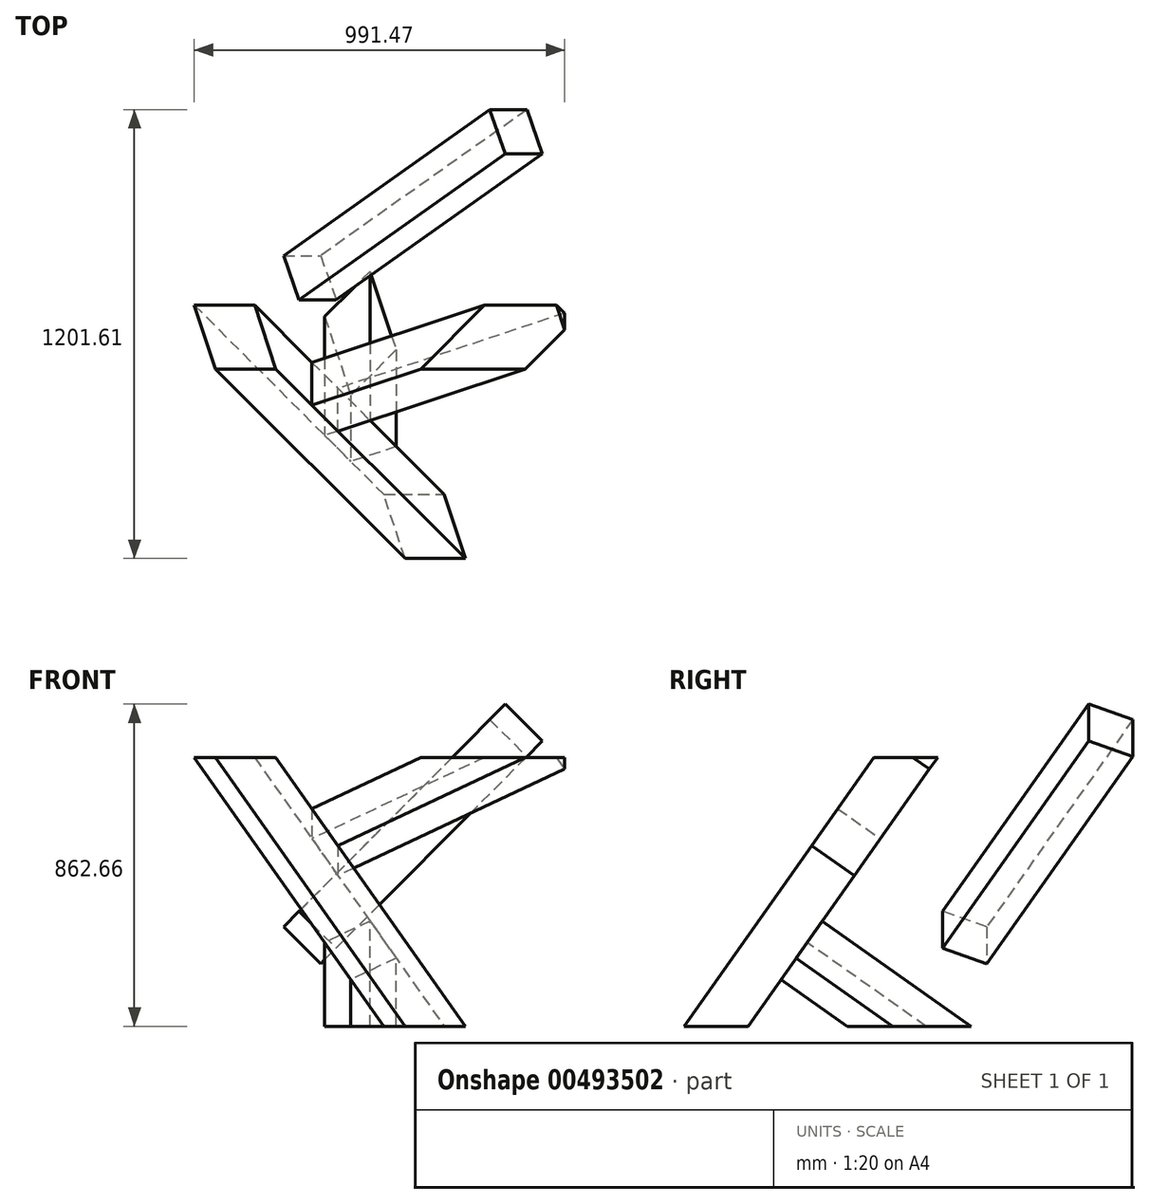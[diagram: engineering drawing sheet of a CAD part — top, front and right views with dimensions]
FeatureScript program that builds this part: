
annotation { "Feature Type Name" : "Feature", "Feature Type Description" : "" }
export const myFeature = defineFeature(function(context is Context, id is Id, definition is map)
    precondition{}
    {
        {
            var Q0;
            Q0=qCreatedBy(makeId("Top.planeOp"),FACE);
            var sketch = newSketch(context, id + "F0", { "sketchPlane" : qUnion([Q0])});
            skLineSegment(sketch, "E0.bottom", {"start": v(400, 400) * mm, "end": v(-400, 400) * mm, "construction": true});
            skLineSegment(sketch, "E0.top", {"start": v(400, -400) * mm, "end": v(-400, -400) * mm, "construction": true});
            skLineSegment(sketch, "E0.left", {"start": v(400, 400) * mm, "end": v(400, -400) * mm, "construction": true});
            skLineSegment(sketch, "E0.right", {"start": v(-400, 400) * mm, "end": v(-400, -400) * mm, "construction": true});
            skPoint(sketch, "E0.middle", {"position": v(0, 0) * mm});
            skPoint(sketch, "E1", {"position": v(250, -314) * mm});
            skSolve(sketch);
        }
        {
            var Q0;
            Q0=qCreatedBy(makeId("Top.planeOp"),FACE);
            cPlane(context, id + "F1", {"entities" : qUnion([Q0]), "cplaneType" : CPlaneType.OFFSET, "offset" : 800 * mm, "width" : 150 * mm, "height" : 150 * mm});
        }
        {
            var Q0;
            Q0=qCreatedBy(id+"F1.planeOp",FACE);
            var sketch = newSketch(context, id + "F2", { "sketchPlane" : qUnion([Q0])});
            skLineSegment(sketch, "E2.0", {"start": v(-400, 400) * mm, "end": v(-400, -400) * mm, "construction": true});
            skLineSegment(sketch, "E2.1", {"start": v(400, 400) * mm, "end": v(-400, 400) * mm, "construction": true});
            skLineSegment(sketch, "E2.2", {"start": v(400, 400) * mm, "end": v(400, -400) * mm, "construction": true});
            skLineSegment(sketch, "E2.3", {"start": v(400, -400) * mm, "end": v(-400, -400) * mm, "construction": true});
            skPoint(sketch, "E3", {"position": v(-314, 250) * mm});
            skSolve(sketch);
        }
        {
            var Q0;
            Q0=sQuery(id+"F2.wireOp",VERTEX,"E3");
            var Q1;
            Q1=sQuery(id+"F0.wireOp",VERTEX,"E1");
            var Q2;
            Q2=sQuery(id+"F2.wireOp",VERTEX,"E2.2.end");
            cPlane(context, id + "F3", {"entities" : qUnion([Q0, Q1, Q2]), "cplaneType" : CPlaneType.THREE_POINT, "offset" : 25 * mm, "width" : 150 * mm, "height" : 150 * mm});
        }
        {
            var Q0;
            Q0=qCreatedBy(id+"F3.planeOp",FACE);
            var sketch = newSketch(context, id + "F4", { "sketchPlane" : qUnion([Q0])});
            skPoint(sketch, "E4.0", {"position": v(366.25, 814.17) * mm});
            skPoint(sketch, "E5.0", {"position": v(-395.76, -19.8) * mm});
            skLineSegment(sketch, "E6", {"start": v(366.25, 814.17) * mm, "end": v(-395.76, -19.8) * mm});
            skLineSegment(sketch, "E7.0", {"start": v(329.34, 847.9) * mm, "end": v(-432.68, 13.92) * mm, "construction": true});
            skSolve(sketch);
        }
        {
            var Q0;
            Q0=sQuery(id+"F4.wireOp",EDGE,"E6");
            cPlane(context, id + "F5", {"entities" : qUnion([Q0]), "cplaneType" : CPlaneType.LINE_ANGLE, "offset" : 25 * mm, "angle" : 0 * degree, "width" : 150 * mm, "height" : 150 * mm});
        }
        {
            var Q0;
            Q0=qCreatedBy(id+"F5.planeOp",FACE);
            var sketch = newSketch(context, id + "F6", { "sketchPlane" : qUnion([Q0])});
            skLineSegment(sketch, "E8.0", {"start": v(-293.32, 809.81) * mm, "end": v(270.68, -169.01) * mm, "construction": true});
            skSolve(sketch);
        }
        {
            var Q0;
            Q0=sQuery(id+"F4.wireOp",VERTEX,"E7.0.start");
            var Q1;
            Q1=sQuery(id+"F4.wireOp",VERTEX,"E4.0");
            var Q2;
            Q2=sQuery(id+"F6.wireOp",VERTEX,"E8.0.start");
            cPlane(context, id + "F7", {"entities" : qUnion([Q0, Q1, Q2]), "cplaneType" : CPlaneType.THREE_POINT, "offset" : 25 * mm, "width" : 150 * mm, "height" : 150 * mm});
        }
        {
            var Q0;
            Q0=qCreatedBy(id+"F7.planeOp",FACE);
            cPlane(context, id + "F8", {"entities" : qUnion([Q0]), "cplaneType" : CPlaneType.OFFSET, "offset" : 565 * mm, "oppositeDirection" : true, "width" : 150 * mm, "height" : 150 * mm});
        }
        {
            var Q0;
            Q0=qCreatedBy(id+"F8.planeOp",FACE);
            var sketch = newSketch(context, id + "F9", { "sketchPlane" : qUnion([Q0])});
            skPoint(sketch, "E9.0", {"position": v(126.29, -256.63) * mm});
            skLineSegment(sketch, "E10.bottom", {"start": v(196.29, -186.63) * mm, "end": v(56.29, -186.63) * mm});
            skLineSegment(sketch, "E10.top", {"start": v(196.29, -326.63) * mm, "end": v(56.29, -326.63) * mm});
            skLineSegment(sketch, "E10.left", {"start": v(196.29, -186.63) * mm, "end": v(196.29, -326.63) * mm});
            skLineSegment(sketch, "E10.right", {"start": v(56.29, -186.63) * mm, "end": v(56.29, -326.63) * mm});
            skSolve(sketch);
        }
        {
            var Q0;
            Q0 = qSketchRegion(id + "F9", true);
            extrude(context, id + "F10", {"entities" : qUnion([Q0]), "depth" : 800 * mm, "hasSecondDirection" : true, "secondDirectionOppositeDirection" : true, "secondDirectionDepth" : 800 * mm});
        }
        {
            var Q0;
            Q0=qCreatedBy(makeId("Right.planeOp"),FACE);
            cPlane(context, id + "F11", {"entities" : qUnion([Q0]), "cplaneType" : CPlaneType.OFFSET, "offset" : 1000 * mm, "oppositeDirection" : true, "width" : 150 * mm, "height" : 150 * mm});
        }
        {
            var Q0;
            Q0=qCreatedBy(id+"F11.planeOp",FACE);
            var sketch = newSketch(context, id + "F12", { "sketchPlane" : qUnion([Q0])});
            skLineSegment(sketch, "E11.0", {"start": v(564.6, 800) * mm, "end": v(0, 800) * mm});
            skLineSegment(sketch, "E12.0", {"start": v(-127.97, 0) * mm, "end": v(-400, 0) * mm});
            skLineSegment(sketch, "E13", {"start": v(564.6, 800) * mm, "end": v(564.6, 1085.03) * mm});
            skLineSegment(sketch, "E14", {"start": v(564.6, 1085.03) * mm, "end": v(0, 1085.03) * mm});
            skLineSegment(sketch, "E15", {"start": v(0, 1085.03) * mm, "end": v(0, 800) * mm});
            skPoint(sketch, "E16.orphan", {"position": v(400, 800) * mm});
            skPoint(sketch, "E17.orphan", {"position": v(-400, 800) * mm});
            skLineSegment(sketch, "E18", {"start": v(-400, 0) * mm, "end": v(-567.88, 0) * mm});
            skLineSegment(sketch, "E19", {"start": v(-567.88, 0) * mm, "end": v(-567.88, -303.64) * mm});
            skLineSegment(sketch, "E20", {"start": v(-567.88, -303.64) * mm, "end": v(-127.97, -303.64) * mm});
            skLineSegment(sketch, "E21", {"start": v(-127.97, -303.64) * mm, "end": v(-127.97, 0) * mm});
            skPoint(sketch, "E22.orphan", {"position": v(400, 0) * mm});
            skSolve(sketch);
        }
        {
            var Q0;
            Q0 = qSketchRegion(id + "F12", true);
            extrude(context, id + "F13", {"entities" : qUnion([Q0]), "operationType" : NewBodyOperationType.REMOVE, "endBound" : BoundingType.THROUGH_ALL, "depth" : 25 * mm});
        }
        {
            var Q0;
            Q0=makeQuery(id+"F10.opExtrude","SWEPT_FACE",FACE,{"disambiguationData":[OSD([sQuery(id+"F9.wireOp",EDGE,"E10.bottom")])]});
            var sketch = newSketch(context, id + "F14", { "sketchPlane" : qUnion([Q0])});
            skLineSegment(sketch, "E23.0", {"start": v(-75.7, 261.8) * mm, "end": v(-145.59, 140.49) * mm});
            skLineSegment(sketch, "E24.0", {"start": v(45.61, 191.9) * mm, "end": v(-24.28, 70.6) * mm});
            skLineSegment(sketch, "E25", {"start": v(-145.59, 140.49) * mm, "end": v(-24.28, 70.6) * mm});
            skLineSegment(sketch, "E26.0", {"start": v(-75.7, 261.8) * mm, "end": v(45.61, 191.9) * mm});
            skPoint(sketch, "E27.orphan", {"position": v(261.65, 847.25) * mm});
            skPoint(sketch, "E28.orphan", {"position": v(423.22, 847.25) * mm});
            skPoint(sketch, "E29.orphan", {"position": v(-140.78, -131.58) * mm});
            skPoint(sketch, "E30.orphan", {"position": v(-302.35, -131.58) * mm});
            skSolve(sketch);
        }
        {
            var Q0;
            Q0 = qSketchRegion(id + "F14", true);
            extrude(context, id + "F15", {"entities" : qUnion([Q0]), "depth" : 700 * mm});
        }
        {
            var Q0;
            Q0=qCreatedBy(id+"F11.planeOp",FACE);
            var sketch = newSketch(context, id + "F16", { "sketchPlane" : qUnion([Q0])});
            skLineSegment(sketch, "E31.bottom", {"start": v(655.93, 0) * mm, "end": v(95.03, 0) * mm});
            skLineSegment(sketch, "E31.top", {"start": v(655.93, -273.26) * mm, "end": v(95.03, -273.26) * mm});
            skLineSegment(sketch, "E31.left", {"start": v(655.93, 0) * mm, "end": v(655.93, -273.26) * mm});
            skLineSegment(sketch, "E31.right", {"start": v(95.03, 0) * mm, "end": v(95.03, -273.26) * mm});
            skSolve(sketch);
        }
        {
            var Q0;
            Q0 = qSketchRegion(id + "F16", true);
            extrude(context, id + "F17", {"entities" : qUnion([Q0]), "operationType" : NewBodyOperationType.REMOVE, "endBound" : BoundingType.THROUGH_ALL, "depth" : 25 * mm});
        }
        {
            var Q0;
            Q0=makeQuery(id+"F10.opExtrude","SWEPT_FACE",FACE,{"disambiguationData":[OSD([sQuery(id+"F9.wireOp",EDGE,"E10.left")])]});
            var sketch = newSketch(context, id + "F18", { "sketchPlane" : qUnion([Q0])});
            skLineSegment(sketch, "E32.0", {"start": v(112.65, 811) * mm, "end": v(-476.24, -153.05) * mm});
            skLineSegment(sketch, "E33.0", {"start": v(291.5, 835.23) * mm, "end": v(-297.39, -128.82) * mm});
            skLineSegment(sketch, "E34", {"start": v(-90.65, 478.19) * mm, "end": v(28.82, 405.2) * mm});
            skLineSegment(sketch, "E35", {"start": v(-17.67, 597.66) * mm, "end": v(101.8, 524.68) * mm});
            skSolve(sketch);
        }
        {
            var Q0;
            {var subQ0=sQuery(id+"F18.wireOp",EDGE,"E34");Q0=makeQuery(id+"F18.imprint","IMPRINT",FACE,{"disambiguationData":[TD([[makeQuery(id+"F18.imprint","IMPRINT",EDGE,{"derivedFrom":subQ0}),1.0]])]});}
            extrude(context, id + "F19", {"entities" : qUnion([Q0]), "depth" : 700 * mm});
        }
        {
            var Q0;
            Q0=qCreatedBy(id+"F11.planeOp",FACE);
            var sketch = newSketch(context, id + "F20", { "sketchPlane" : qUnion([Q0])});
            skLineSegment(sketch, "E36.0", {"start": v(468.48, 800) * mm, "end": v(400, 800) * mm});
            skLineSegment(sketch, "E37", {"start": v(468.48, 800) * mm, "end": v(468.48, 1033.91) * mm});
            skLineSegment(sketch, "E38", {"start": v(468.48, 1033.91) * mm, "end": v(129.15, 1033.91) * mm});
            skLineSegment(sketch, "E39", {"start": v(129.15, 1033.91) * mm, "end": v(129.15, 800) * mm});
            skPoint(sketch, "E40.orphan", {"position": v(400, 800) * mm});
            skPoint(sketch, "E41.orphan", {"position": v(-400, 800) * mm});
            skLineSegment(sketch, "E42", {"start": v(400, 800) * mm, "end": v(129.15, 800) * mm});
            skSolve(sketch);
        }
        {
            var Q0;
            Q0 = qSketchRegion(id + "F20", true);
            extrude(context, id + "F21", {"entities" : qUnion([Q0]), "operationType" : NewBodyOperationType.REMOVE, "endBound" : BoundingType.THROUGH_ALL, "depth" : 25 * mm});
        }
        {
            var Q0;
            Q0=qCreatedBy(id+"F11.planeOp",FACE);
            var sketch = newSketch(context, id + "F22", { "sketchPlane" : qUnion([Q0])});
            skLineSegment(sketch, "E43.0", {"start": v(400, 800) * mm, "end": v(-400, 800) * mm, "construction": true});
            skLineSegment(sketch, "E44.0", {"start": v(400, 0) * mm, "end": v(-400, 0) * mm, "construction": true});
            skLineSegment(sketch, "E45.0", {"start": v(400, 760) * mm, "end": v(-400, 760) * mm});
            skLineSegment(sketch, "E46.0", {"start": v(497.86, 40) * mm, "end": v(-483.43, 40) * mm});
            skLineSegment(sketch, "E47", {"start": v(400, 760) * mm, "end": v(400, 856.38) * mm});
            skLineSegment(sketch, "E48", {"start": v(400, 856.38) * mm, "end": v(-400, 856.38) * mm});
            skLineSegment(sketch, "E49", {"start": v(-400, 856.38) * mm, "end": v(-400, 760) * mm});
            skLineSegment(sketch, "E50", {"start": v(497.86, 40) * mm, "end": v(497.86, -63.05) * mm});
            skLineSegment(sketch, "E51", {"start": v(497.86, -63.05) * mm, "end": v(-483.43, -63.05) * mm});
            skLineSegment(sketch, "E52", {"start": v(-483.43, -63.05) * mm, "end": v(-483.43, 40) * mm});
            skPoint(sketch, "E53.orphan", {"position": v(400, 40) * mm});
            skPoint(sketch, "E54.orphan", {"position": v(-400, 40) * mm});
            skSolve(sketch);
        }
        {
            var Q0;
            Q0 = qSketchRegion(id + "F22", true);
            extrude(context, id + "F23", {"entities" : qUnion([Q0]), "operationType" : NewBodyOperationType.REMOVE, "endBound" : BoundingType.THROUGH_ALL, "depth" : 25 * mm});
        }
        {
            var Q0;
            Q0=makeQuery(id+"F10.opExtrude","SWEPT_FACE",FACE,{"disambiguationData":[OSD([sQuery(id+"F9.wireOp",EDGE,"E10.left")])]});
            var sketch = newSketch(context, id + "F24", { "sketchPlane" : qUnion([Q0])});
            skLineSegment(sketch, "E55.0", {"start": v(-47.12, 549.46) * mm, "end": v(-120.62, 429.13) * mm});
            skLineSegment(sketch, "E55.1", {"start": v(72.36, 476.48) * mm, "end": v(-1.15, 356.15) * mm});
            skLineSegment(sketch, "E56", {"start": v(-47.12, 549.46) * mm, "end": v(72.36, 476.48) * mm});
            skLineSegment(sketch, "E57.0", {"start": v(-120.62, 429.13) * mm, "end": v(-1.15, 356.15) * mm});
            skPoint(sketch, "E58.orphan", {"position": v(83.2, 762.8) * mm});
            skPoint(sketch, "E59.orphan", {"position": v(262.06, 787.03) * mm});
            skPoint(sketch, "E60.orphan", {"position": v(-267.94, -80.62) * mm});
            skPoint(sketch, "E61.orphan", {"position": v(-446.8, -104.85) * mm});
            skSolve(sketch);
        }
        {
            var Q0;
            Q0=makeQuery(id+"F10.opExtrude","SWEPT_FACE",FACE,{"disambiguationData":[OSD([sQuery(id+"F9.wireOp",EDGE,"E10.top")])]});
            var sketch = newSketch(context, id + "F25", { "sketchPlane" : qUnion([Q0])});
            skLineSegment(sketch, "E62.0", {"start": v(-51.76, 483) * mm, "end": v(18.63, 360.82) * mm});
            skLineSegment(sketch, "E63", {"start": v(-51.76, 483) * mm, "end": v(56.82, 394.62) * mm});
            skLineSegment(sketch, "E64", {"start": v(56.82, 394.62) * mm, "end": v(18.63, 360.82) * mm});
            skSolve(sketch);
        }
        {
            var Q0;
            Q0=sQuery(id+"F24.wireOp",VERTEX,"E56.end");
            var Q1;
            Q1=sQuery(id+"F25.wireOp",VERTEX,"E63.start");
            var Q2;
            Q2=sQuery(id+"F25.wireOp",VERTEX,"E64.start");
            cPlane(context, id + "F26", {"entities" : qUnion([Q0, Q1, Q2]), "cplaneType" : CPlaneType.THREE_POINT, "offset" : 25 * mm, "width" : 150 * mm, "height" : 150 * mm});
        }
        {
            var Q0;
            Q0=qCreatedBy(id+"F26.planeOp",FACE);
            var sketch = newSketch(context, id + "F27", { "sketchPlane" : qUnion([Q0])});
            skLineSegment(sketch, "E65.0", {"start": v(-345.02, 326.63) * mm, "end": v(-345.02, 186.63) * mm});
            skLineSegment(sketch, "E65.1", {"start": v(-345.02, 326.63) * mm, "end": v(-205.02, 326.63) * mm});
            skLineSegment(sketch, "E66.0", {"start": v(-345.02, 186.63) * mm, "end": v(-213.3, 186.63) * mm});
            skLineSegment(sketch, "E67.0", {"start": v(-213.3, 326.63) * mm, "end": v(-213.3, 186.63) * mm});
            skSolve(sketch);
        }
        {
            var Q0;
            Q0=makeQuery(id+"F27.imprint","IMPRINT",FACE,{"disambiguationData":[TD([[makeQuery(id+"F27.imprint","IMPRINT",EDGE,{"derivedFrom":sQuery(id+"F27.wireOp",EDGE,"E65.0")}),1.0]])]});
            extrude(context, id + "F28", {"entities" : qUnion([Q0]), "operationType" : NewBodyOperationType.ADD, "oppositeDirection" : true, "depth" : 25 * mm, "hasSecondDirection" : true, "secondDirectionOppositeDirection" : false, "secondDirectionDepth" : 50 * mm});
        }
        {
            var Q0;
            Q0=makeQuery(id+"F28.opExtrude","CAP_FACE",FACE,{"disambiguationData":[OSD([sQuery(id+"F27.wireOp",EDGE,"E65.0"),sQuery(id+"F27.wireOp",EDGE,"E65.1"),sQuery(id+"F27.wireOp",EDGE,"E66.0"),sQuery(id+"F27.wireOp",EDGE,"E67.0")])],"isStart":false});
            extrude(context, id + "F29", {"entities" : qUnion([Q0]), "operationType" : NewBodyOperationType.ADD, "depth" : 800 * mm});
        }
        {
            var Q0;
            Q0=qCreatedBy(id+"F11.planeOp",FACE);
            var sketch = newSketch(context, id + "F30", { "sketchPlane" : qUnion([Q0])});
            skLineSegment(sketch, "E68.0", {"start": v(136.15, 760) * mm, "end": v(307.45, 760) * mm});
            skLineSegment(sketch, "E68.1", {"start": v(380.04, 1105.94) * mm, "end": v(494.46, 1025.27) * mm});
            skLineSegment(sketch, "E69", {"start": v(307.45, 760) * mm, "end": v(494.46, 1025.27) * mm});
            skLineSegment(sketch, "E70", {"start": v(136.15, 760) * mm, "end": v(380.04, 1105.94) * mm});
            skSolve(sketch);
        }
        {
            var Q0;
            Q0=makeQuery(id+"F30.imprint","IMPRINT",FACE,{"disambiguationData":[TD([[makeQuery(id+"F30.imprint","IMPRINT",EDGE,{"derivedFrom":sQuery(id+"F30.wireOp",EDGE,"E68.0")}),1.0]])]});
            extrude(context, id + "F31", {"entities" : qUnion([Q0]), "operationType" : NewBodyOperationType.REMOVE, "endBound" : BoundingType.THROUGH_ALL, "depth" : 25 * mm});
        }
    });
